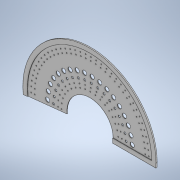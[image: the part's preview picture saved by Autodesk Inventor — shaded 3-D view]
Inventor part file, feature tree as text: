
AUTODESK INVENTOR PART (.ipt)
format: ipt  version: 2021.2 (Build 252289000, 289)  size: 380,928 bytes
history: native  units: in
note: dims shown in document units (in); Inventor stores cm internally (conversion verified against a paired STEP export)
features: extrude x4, sketch x4, pattern_circular x2
ambient origin geometry x8: Origin, YZ Plane, XZ Plane, XY Plane, X Axis, Y Axis, Z Axis, Center Point
bodies: Solid1 (feature_tree)
feature tree (10):
  extrude  "Extrusion1"  Depth=1.3306in
  extrude  "Extrusion2"  Depth=3.5806in
  extrude  "Extrusion3"  Depth=3.8306in
  pattern_circular  "Circular Pattern1"  [2 undecoded]
  extrude  "Extrusion4"  Depth=0.0625in
  pattern_circular  "Circular Pattern2"  [2 undecoded]
  sketch  "Sketch1"  dims[d2=1.3306in d3=1.2781in]
  sketch  "Sketch2"  dims[d4=3.5806in d5=1.2781in]
  sketch  "Sketch3"  dims[d6=0.0312in d7=0.0in d10=3.8306in]
  sketch  "Sketch4"  dims[d11=0.0625in d12=0.0in d13=0.25in d14=0.0625in d15=0.0625in d18=0.1in d19=0.1in d20=0.0in d21=0.0in d22=14.1732in d23=180.0deg d25=0.25in d26=0.125in d27=0.0625in d28=0.0625in d29=0.2in d30=0.2in d31=0.2in d32=0.2in d34=0.2in d35=0.4in d36=0.75in d37=0.5in d38=0.3in d39=0.0625in d40=0.0in d41=7.0866in d42=1.2025in d44=0.75in]
note: 4 required parameter values undecoded (feature->parameter linkage not recoverable at this tier; creation-order binding heuristic only, values carry confidence <= 0.55)
